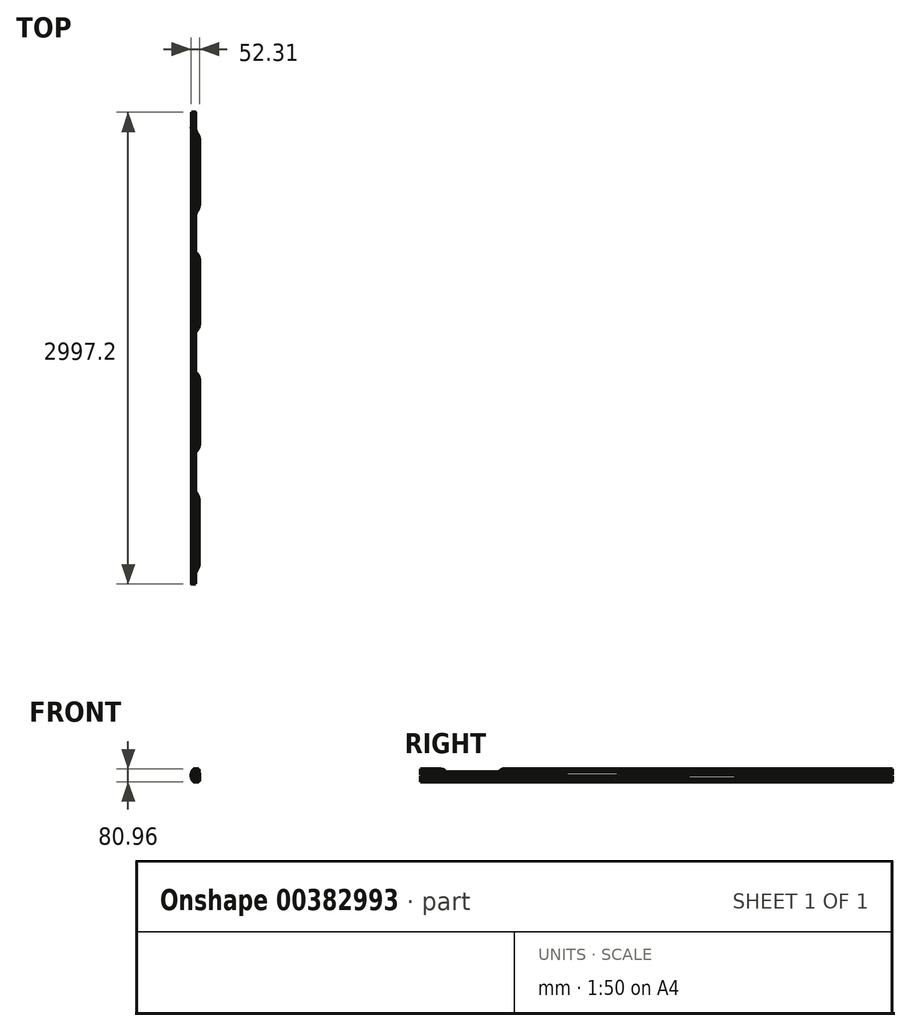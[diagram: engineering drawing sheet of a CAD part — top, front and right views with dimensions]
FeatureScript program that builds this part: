
annotation { "Feature Type Name" : "Feature", "Feature Type Description" : "" }
export const myFeature = defineFeature(function(context is Context, id is Id, definition is map)
    precondition{}
    {
        {
            var Q0;
            Q0=qCreatedBy(makeId("Front.planeOp"),FACE);
            var sketch = newSketch(context, id + "F0", { "sketchPlane" : qUnion([Q0])});
            skCircle(sketch, "E0", {"center": v(0, 0) * mm, "radius": 66.68 * mm});
            skLineSegment(sketch, "E1", {"start": v(0, 0) * mm, "end": v(0, 66.68) * mm});
            skLineSegment(sketch, "E2", {"start": v(0, 66.68) * mm, "end": v(0, 0) * mm});
            skLineSegment(sketch, "E3", {"start": v(0, -66.68) * mm, "end": v(0, 0) * mm});
            skCircle(sketch, "E4.0", {"center": v(0, 0) * mm, "radius": 53.98 * mm});
            skLineSegment(sketch, "E5", {"start": v(0, 0) * mm, "end": v(-53.98, 0) * mm});
            skLineSegment(sketch, "E6.3.0", {"start": v(0, 0) * mm, "end": v(0, -53.98) * mm});
            skLineSegment(sketch, "E6.anchor1", {"start": v(0, 0) * mm, "end": v(-53.98, 0) * mm, "construction": true});
            skLineSegment(sketch, "E6.anchor2", {"start": v(0, 0) * mm, "end": v(0, -53.98) * mm, "construction": true});
            skCircle(sketch, "E7", {"center": v(-44.21, 30.96) * mm, "radius": 9.53 * mm});
            skCircle(sketch, "E8", {"center": v(-52.7, 11.68) * mm, "radius": 9.53 * mm});
            skCircle(sketch, "E9", {"center": v(-52.7, -11.68) * mm, "radius": 9.53 * mm});
            skCircle(sketch, "E10", {"center": v(-44.21, -30.96) * mm, "radius": 9.53 * mm});
            skLineSegment(sketch, "E11", {"start": v(0, 0) * mm, "end": v(-44.21, 30.96) * mm});
            skLineSegment(sketch, "E12", {"start": v(-44.21, 30.96) * mm, "end": v(-52.02, 36.42) * mm});
            skLineSegment(sketch, "E13", {"start": v(0, 0) * mm, "end": v(-52.7, 11.68) * mm});
            skLineSegment(sketch, "E14", {"start": v(0, 0) * mm, "end": v(-52.7, -11.68) * mm});
            skLineSegment(sketch, "E15", {"start": v(0, 0) * mm, "end": v(-44.21, -30.96) * mm});
            skLineSegment(sketch, "E16", {"start": v(-44.21, -30.96) * mm, "end": v(-52.02, -36.42) * mm});
            skLineSegment(sketch, "E17", {"start": v(-44.21, 30.96) * mm, "end": v(-36.41, 25.5) * mm});
            skPoint(sketch, "E18", {"position": v(-43.4, 9.62) * mm});
            skPoint(sketch, "E19", {"position": v(-43.4, -9.62) * mm});
            skPoint(sketch, "E20", {"position": v(-36.41, -25.5) * mm});
            skArc(sketch, "E21", {"start": v(-36.41, 25.5) * mm, "mid": v(-44.45, 0) * mm, "end": v(-36.41, -25.5) * mm});
            skArc(sketch, "E22", {"start": v(-52.02, 36.42) * mm, "mid": v(-63.5, 0) * mm, "end": v(-52.02, -36.42) * mm});
            skSolve(sketch);
        }
        {
            var Q0;
            {var subQ0=sQuery(id+"F0.wireOp",EDGE,"E17");Q0=makeQuery(id+"F0.imprint","IMPRINT",FACE,{"disambiguationData":[TD([[makeQuery(id+"F0.imprint","IMPRINT",EDGE,{"derivedFrom":subQ0}),1.0]])]});}
            var Q1;
            {var subQ0=sQuery(id+"F0.wireOp",EDGE,"E12");Q1=makeQuery(id+"F0.imprint","IMPRINT",FACE,{"disambiguationData":[TD([[makeQuery(id+"F0.imprint","IMPRINT",EDGE,{"derivedFrom":subQ0}),-1.0]])]});}
            var Q2;
            {var subQ0=sQuery(id+"F0.wireOp",EDGE,"E12");Q2=makeQuery(id+"F0.imprint","IMPRINT",FACE,{"disambiguationData":[TD([[makeQuery(id+"F0.imprint","IMPRINT",EDGE,{"derivedFrom":subQ0}),1.0]])]});}
            var Q3;
            {var subQ0=sQuery(id+"F0.wireOp",EDGE,"E17");Q3=makeQuery(id+"F0.imprint","IMPRINT",FACE,{"disambiguationData":[TD([[makeQuery(id+"F0.imprint","IMPRINT",EDGE,{"derivedFrom":subQ0}),-1.0]])]});}
            var Q4;
            {var subQ0=sQuery(id+"F0.wireOp",EDGE,"E7");var subQ1=sQuery(id+"F0.wireOp",EDGE,"E4.0");var subQ2=makeQuery(id+"F0.imprint","INTERSECT",VERTEX,{"disambiguationData":[OD(1.0)],"derivedFrom":[subQ1,subQ0]});Q4=makeQuery(id+"F0.imprint","IMPRINT",FACE,{"disambiguationData":[TD([[makeQuery(id+"F0.imprint","IMPRINT",EDGE,{"disambiguationData":[TD([[subQ2,-1.0]])],"derivedFrom":subQ1}),-1.0]])]});}
            var Q5;
            {var subQ0=sQuery(id+"F0.wireOp",EDGE,"E7");var subQ1=sQuery(id+"F0.wireOp",EDGE,"E4.0");var subQ2=makeQuery(id+"F0.imprint","INTERSECT",VERTEX,{"disambiguationData":[OD(1.0)],"derivedFrom":[subQ1,subQ0]});Q5=makeQuery(id+"F0.imprint","IMPRINT",FACE,{"disambiguationData":[TD([[makeQuery(id+"F0.imprint","IMPRINT",EDGE,{"disambiguationData":[TD([[subQ2,-1.0]])],"derivedFrom":subQ1}),1.0]])]});}
            var Q6;
            {var subQ0=sQuery(id+"F0.wireOp",EDGE,"E13");var subQ1=sQuery(id+"F0.wireOp",EDGE,"E4.0");var subQ2=makeQuery(id+"F0.imprint","INTERSECT",VERTEX,{"derivedFrom":[subQ1,subQ0]});Q6=makeQuery(id+"F0.imprint","IMPRINT",FACE,{"disambiguationData":[TD([[makeQuery(id+"F0.imprint","IMPRINT",EDGE,{"disambiguationData":[TD([[subQ2,1.0]])],"derivedFrom":subQ1}),1.0]])]});}
            var Q7;
            {var subQ0=sQuery(id+"F0.wireOp",EDGE,"E4.0");var subQ1=makeQuery(id+"F0.imprint","INTERSECT",VERTEX,{"derivedFrom":[subQ0,sQuery(id+"F0.wireOp",EDGE,"E13")]});Q7=makeQuery(id+"F0.imprint","IMPRINT",FACE,{"disambiguationData":[TD([[makeQuery(id+"F0.imprint","IMPRINT",EDGE,{"disambiguationData":[TD([[subQ1,1.0]])],"derivedFrom":subQ0}),-1.0]])]});}
            var Q8;
            {var subQ0=sQuery(id+"F0.wireOp",EDGE,"E13");var subQ1=sQuery(id+"F0.wireOp",EDGE,"E4.0");var subQ2=makeQuery(id+"F0.imprint","INTERSECT",VERTEX,{"derivedFrom":[subQ1,subQ0]});Q8=makeQuery(id+"F0.imprint","IMPRINT",FACE,{"disambiguationData":[TD([[makeQuery(id+"F0.imprint","IMPRINT",EDGE,{"disambiguationData":[TD([[subQ2,-1.0]])],"derivedFrom":subQ1}),1.0]])]});}
            var Q9;
            {var subQ1=sQuery(id+"F0.wireOp",EDGE,"E4.0");var subQ8=makeQuery(id+"F0.imprint","INTERSECT",VERTEX,{"derivedFrom":[subQ1,sQuery(id+"F0.wireOp",EDGE,"E5")]});Q9=makeQuery(id+"F0.imprint","IMPRINT",FACE,{"disambiguationData":[TD([[makeQuery(id+"F0.imprint","IMPRINT",EDGE,{"disambiguationData":[TD([[subQ8,1.0]])],"derivedFrom":subQ1}),-1.0]])]});}
            var Q10;
            {var subQ0=sQuery(id+"F0.wireOp",EDGE,"E5");var subQ1=sQuery(id+"F0.wireOp",EDGE,"E4.0");var subQ2=makeQuery(id+"F0.imprint","INTERSECT",VERTEX,{"derivedFrom":[subQ1,subQ0]});Q10=makeQuery(id+"F0.imprint","IMPRINT",FACE,{"disambiguationData":[TD([[makeQuery(id+"F0.imprint","IMPRINT",EDGE,{"disambiguationData":[TD([[subQ2,1.0]])],"derivedFrom":subQ1}),1.0]])]});}
            var Q11;
            {var subQ0=sQuery(id+"F0.wireOp",EDGE,"E5");var subQ1=sQuery(id+"F0.wireOp",EDGE,"E4.0");var subQ2=makeQuery(id+"F0.imprint","INTERSECT",VERTEX,{"derivedFrom":[subQ1,subQ0]});Q11=makeQuery(id+"F0.imprint","IMPRINT",FACE,{"disambiguationData":[TD([[makeQuery(id+"F0.imprint","IMPRINT",EDGE,{"disambiguationData":[TD([[subQ2,-1.0]])],"derivedFrom":subQ1}),1.0]])]});}
            var Q12;
            {var subQ0=sQuery(id+"F0.wireOp",EDGE,"E4.0");var subQ1=makeQuery(id+"F0.imprint","INTERSECT",VERTEX,{"derivedFrom":[subQ0,sQuery(id+"F0.wireOp",EDGE,"E14")]});Q12=makeQuery(id+"F0.imprint","IMPRINT",FACE,{"disambiguationData":[TD([[makeQuery(id+"F0.imprint","IMPRINT",EDGE,{"disambiguationData":[TD([[subQ1,1.0]])],"derivedFrom":subQ0}),-1.0]])]});}
            var Q13;
            {var subQ0=sQuery(id+"F0.wireOp",EDGE,"E14");var subQ1=sQuery(id+"F0.wireOp",EDGE,"E4.0");var subQ2=makeQuery(id+"F0.imprint","INTERSECT",VERTEX,{"derivedFrom":[subQ1,subQ0]});Q13=makeQuery(id+"F0.imprint","IMPRINT",FACE,{"disambiguationData":[TD([[makeQuery(id+"F0.imprint","IMPRINT",EDGE,{"disambiguationData":[TD([[subQ2,-1.0]])],"derivedFrom":subQ1}),1.0]])]});}
            var Q14;
            {var subQ0=sQuery(id+"F0.wireOp",EDGE,"E9");var subQ1=sQuery(id+"F0.wireOp",EDGE,"E4.0");var subQ2=makeQuery(id+"F0.imprint","INTERSECT",VERTEX,{"disambiguationData":[OD(1.0)],"derivedFrom":[subQ1,subQ0]});Q14=makeQuery(id+"F0.imprint","IMPRINT",FACE,{"disambiguationData":[TD([[makeQuery(id+"F0.imprint","IMPRINT",EDGE,{"disambiguationData":[TD([[subQ2,-1.0]])],"derivedFrom":subQ1}),1.0]])]});}
            var Q15;
            {var subQ0=sQuery(id+"F0.wireOp",EDGE,"E9");var subQ1=sQuery(id+"F0.wireOp",EDGE,"E4.0");var subQ2=makeQuery(id+"F0.imprint","INTERSECT",VERTEX,{"disambiguationData":[OD(1.0)],"derivedFrom":[subQ1,subQ0]});Q15=makeQuery(id+"F0.imprint","IMPRINT",FACE,{"disambiguationData":[TD([[makeQuery(id+"F0.imprint","IMPRINT",EDGE,{"disambiguationData":[TD([[subQ2,-1.0]])],"derivedFrom":subQ1}),-1.0]])]});}
            var Q16;
            {var subQ0=sQuery(id+"F0.wireOp",EDGE,"E16");Q16=makeQuery(id+"F0.imprint","IMPRINT",FACE,{"disambiguationData":[TD([[makeQuery(id+"F0.imprint","IMPRINT",EDGE,{"derivedFrom":subQ0}),-1.0]])]});}
            var Q17;
            {var subQ1=sQuery(id+"F0.wireOp",EDGE,"E4.0");var subQ3=sQuery(id+"F0.wireOp",EDGE,"E10");var subQ4=makeQuery(id+"F0.imprint","INTERSECT",VERTEX,{"disambiguationData":[OD(0.0)],"derivedFrom":[subQ1,subQ3]});Q17=makeQuery(id+"F0.imprint","IMPRINT",FACE,{"disambiguationData":[TD([[makeQuery(id+"F0.imprint","IMPRINT",EDGE,{"disambiguationData":[TD([[subQ4,-1.0]])],"derivedFrom":subQ1}),1.0]])]});}
            var Q18;
            {var subQ1=sQuery(id+"F0.wireOp",EDGE,"E4.0");var subQ3=sQuery(id+"F0.wireOp",EDGE,"E10");var subQ4=makeQuery(id+"F0.imprint","INTERSECT",VERTEX,{"disambiguationData":[OD(1.0)],"derivedFrom":[subQ1,subQ3]});Q18=makeQuery(id+"F0.imprint","IMPRINT",FACE,{"disambiguationData":[TD([[makeQuery(id+"F0.imprint","IMPRINT",EDGE,{"disambiguationData":[TD([[subQ4,1.0]])],"derivedFrom":subQ1}),1.0]])]});}
            var Q19;
            {var subQ0=sQuery(id+"F0.wireOp",EDGE,"E16");Q19=makeQuery(id+"F0.imprint","IMPRINT",FACE,{"disambiguationData":[TD([[makeQuery(id+"F0.imprint","IMPRINT",EDGE,{"derivedFrom":subQ0}),1.0]])]});}
            var Q20;
            {var subQ0=sQuery(id+"F0.wireOp",EDGE,"E14");var subQ1=sQuery(id+"F0.wireOp",EDGE,"E4.0");var subQ2=makeQuery(id+"F0.imprint","INTERSECT",VERTEX,{"derivedFrom":[subQ1,subQ0]});Q20=makeQuery(id+"F0.imprint","IMPRINT",FACE,{"disambiguationData":[TD([[makeQuery(id+"F0.imprint","IMPRINT",EDGE,{"disambiguationData":[TD([[subQ2,1.0]])],"derivedFrom":subQ1}),1.0]])]});}
            extrude(context, id + "F1", {"entities" : qUnion([Q0, Q1, Q2, Q3, Q4, Q5, Q6, Q7, Q8, Q9, Q10, Q11, Q12, Q13, Q14, Q15, Q16, Q17, Q18, Q19, Q20]), "oppositeDirection" : true, "depth" : 3.17 * mm});
        }
        {
            var Q0;
            {var subQ0=sQuery(id+"F0.wireOp",EDGE,"E12");Q0=makeQuery(id+"F0.imprint","IMPRINT",FACE,{"disambiguationData":[TD([[makeQuery(id+"F0.imprint","IMPRINT",EDGE,{"derivedFrom":subQ0}),1.0]])]});}
            var Q1;
            {var subQ0=sQuery(id+"F0.wireOp",EDGE,"E12");Q1=makeQuery(id+"F0.imprint","IMPRINT",FACE,{"disambiguationData":[TD([[makeQuery(id+"F0.imprint","IMPRINT",EDGE,{"derivedFrom":subQ0}),-1.0]])]});}
            var Q2;
            {var subQ0=sQuery(id+"F0.wireOp",EDGE,"E17");Q2=makeQuery(id+"F0.imprint","IMPRINT",FACE,{"disambiguationData":[TD([[makeQuery(id+"F0.imprint","IMPRINT",EDGE,{"derivedFrom":subQ0}),1.0]])]});}
            var Q3;
            {var subQ0=sQuery(id+"F0.wireOp",EDGE,"E17");Q3=makeQuery(id+"F0.imprint","IMPRINT",FACE,{"disambiguationData":[TD([[makeQuery(id+"F0.imprint","IMPRINT",EDGE,{"derivedFrom":subQ0}),-1.0]])]});}
            var Q4;
            {var subQ0=sQuery(id+"F0.wireOp",EDGE,"E13");var subQ1=sQuery(id+"F0.wireOp",EDGE,"E4.0");var subQ2=makeQuery(id+"F0.imprint","INTERSECT",VERTEX,{"derivedFrom":[subQ1,subQ0]});Q4=makeQuery(id+"F0.imprint","IMPRINT",FACE,{"disambiguationData":[TD([[makeQuery(id+"F0.imprint","IMPRINT",EDGE,{"disambiguationData":[TD([[subQ2,1.0]])],"derivedFrom":subQ1}),1.0]])]});}
            var Q5;
            {var subQ0=sQuery(id+"F0.wireOp",EDGE,"E13");var subQ1=sQuery(id+"F0.wireOp",EDGE,"E4.0");var subQ2=makeQuery(id+"F0.imprint","INTERSECT",VERTEX,{"derivedFrom":[subQ1,subQ0]});Q5=makeQuery(id+"F0.imprint","IMPRINT",FACE,{"disambiguationData":[TD([[makeQuery(id+"F0.imprint","IMPRINT",EDGE,{"disambiguationData":[TD([[subQ2,-1.0]])],"derivedFrom":subQ1}),1.0]])]});}
            var Q6;
            {var subQ0=sQuery(id+"F0.wireOp",EDGE,"E4.0");var subQ1=makeQuery(id+"F0.imprint","INTERSECT",VERTEX,{"derivedFrom":[subQ0,sQuery(id+"F0.wireOp",EDGE,"E13")]});Q6=makeQuery(id+"F0.imprint","IMPRINT",FACE,{"disambiguationData":[TD([[makeQuery(id+"F0.imprint","IMPRINT",EDGE,{"disambiguationData":[TD([[subQ1,1.0]])],"derivedFrom":subQ0}),-1.0]])]});}
            var Q7;
            {var subQ0=sQuery(id+"F0.wireOp",EDGE,"E4.0");var subQ1=makeQuery(id+"F0.imprint","INTERSECT",VERTEX,{"derivedFrom":[subQ0,sQuery(id+"F0.wireOp",EDGE,"E14")]});Q7=makeQuery(id+"F0.imprint","IMPRINT",FACE,{"disambiguationData":[TD([[makeQuery(id+"F0.imprint","IMPRINT",EDGE,{"disambiguationData":[TD([[subQ1,1.0]])],"derivedFrom":subQ0}),-1.0]])]});}
            var Q8;
            {var subQ0=sQuery(id+"F0.wireOp",EDGE,"E14");var subQ1=sQuery(id+"F0.wireOp",EDGE,"E4.0");var subQ2=makeQuery(id+"F0.imprint","INTERSECT",VERTEX,{"derivedFrom":[subQ1,subQ0]});Q8=makeQuery(id+"F0.imprint","IMPRINT",FACE,{"disambiguationData":[TD([[makeQuery(id+"F0.imprint","IMPRINT",EDGE,{"disambiguationData":[TD([[subQ2,1.0]])],"derivedFrom":subQ1}),1.0]])]});}
            var Q9;
            {var subQ0=sQuery(id+"F0.wireOp",EDGE,"E14");var subQ1=sQuery(id+"F0.wireOp",EDGE,"E4.0");var subQ2=makeQuery(id+"F0.imprint","INTERSECT",VERTEX,{"derivedFrom":[subQ1,subQ0]});Q9=makeQuery(id+"F0.imprint","IMPRINT",FACE,{"disambiguationData":[TD([[makeQuery(id+"F0.imprint","IMPRINT",EDGE,{"disambiguationData":[TD([[subQ2,-1.0]])],"derivedFrom":subQ1}),1.0]])]});}
            var Q10;
            {var subQ0=sQuery(id+"F0.wireOp",EDGE,"E16");Q10=makeQuery(id+"F0.imprint","IMPRINT",FACE,{"disambiguationData":[TD([[makeQuery(id+"F0.imprint","IMPRINT",EDGE,{"derivedFrom":subQ0}),-1.0]])]});}
            var Q11;
            {var subQ0=sQuery(id+"F0.wireOp",EDGE,"E16");Q11=makeQuery(id+"F0.imprint","IMPRINT",FACE,{"disambiguationData":[TD([[makeQuery(id+"F0.imprint","IMPRINT",EDGE,{"derivedFrom":subQ0}),1.0]])]});}
            var Q12;
            {var subQ1=sQuery(id+"F0.wireOp",EDGE,"E4.0");var subQ3=sQuery(id+"F0.wireOp",EDGE,"E10");var subQ4=makeQuery(id+"F0.imprint","INTERSECT",VERTEX,{"disambiguationData":[OD(1.0)],"derivedFrom":[subQ1,subQ3]});Q12=makeQuery(id+"F0.imprint","IMPRINT",FACE,{"disambiguationData":[TD([[makeQuery(id+"F0.imprint","IMPRINT",EDGE,{"disambiguationData":[TD([[subQ4,1.0]])],"derivedFrom":subQ1}),1.0]])]});}
            var Q13;
            {var subQ1=sQuery(id+"F0.wireOp",EDGE,"E4.0");var subQ3=sQuery(id+"F0.wireOp",EDGE,"E10");var subQ4=makeQuery(id+"F0.imprint","INTERSECT",VERTEX,{"disambiguationData":[OD(0.0)],"derivedFrom":[subQ1,subQ3]});Q13=makeQuery(id+"F0.imprint","IMPRINT",FACE,{"disambiguationData":[TD([[makeQuery(id+"F0.imprint","IMPRINT",EDGE,{"disambiguationData":[TD([[subQ4,-1.0]])],"derivedFrom":subQ1}),1.0]])]});}
            extrude(context, id + "F2", {"entities" : qUnion([Q0, Q1, Q2, Q3, Q4, Q5, Q6, Q7, Q8, Q9, Q10, Q11, Q12, Q13]), "operationType" : NewBodyOperationType.ADD, "oppositeDirection" : true, "depth" : 101.6 * mm});
        }
        {
            var Q0;
            Q0=qCreatedBy(makeId("Top.planeOp"),FACE);
            var sketch = newSketch(context, id + "F3", { "sketchPlane" : qUnion([Q0])});
            skPoint(sketch, "E23.0", {"position": v(-44.21, 0) * mm});
            skPoint(sketch, "E24", {"position": v(-20.72, -76.2) * mm});
            skFitSpline(sketch, "E25", {"points": [v(-44.21, 0) * mm, v(-20.72, -76.2) * mm], "startDerivative": vector(0, -114.3) * mm, "endDerivative": vector(0, -114.3) * mm});
            skLineSegment(sketch, "E26", {"start": v(-20.72, -76.2) * mm, "end": v(-20.72, -482.6) * mm});
            skPoint(sketch, "E27", {"position": v(-44.21, -482.6) * mm});
            skPoint(sketch, "E28", {"position": v(-44.21, -520.7) * mm});
            skPoint(sketch, "E29", {"position": v(-44.21, -558.8) * mm});
            skFitSpline(sketch, "E30", {"points": [v(-44.21, -558.8) * mm, v(-20.72, -482.6) * mm], "startDerivative": vector(0, 114.3) * mm, "endDerivative": vector(0, 114.3) * mm});
            skLineSegment(sketch, "E31", {"start": v(-44.21, -558.8) * mm, "end": v(-44.21, -2895.6) * mm});
            skPoint(sketch, "E32.0", {"position": v(-52.7, 0) * mm});
            skLineSegment(sketch, "E33", {"start": v(-52.7, 0) * mm, "end": v(-52.7, -762) * mm});
            skLineSegment(sketch, "E34", {"start": v(-52.7, -762) * mm, "end": v(-52.7, -838.2) * mm});
            skLineSegment(sketch, "E35", {"start": v(-52.7, -838.2) * mm, "end": v(-20.72, -838.2) * mm});
            skLineSegment(sketch, "E36", {"start": v(-20.72, -1244.6) * mm, "end": v(-52.7, -1244.6) * mm});
            skLineSegment(sketch, "E37", {"start": v(-52.7, -1244.6) * mm, "end": v(-52.7, -2895.6) * mm});
            skLineSegment(sketch, "E38", {"start": v(-52.7, -1244.6) * mm, "end": v(-52.7, -1320.8) * mm});
            skLineSegment(sketch, "E39", {"start": v(-52.7, -1320.8) * mm, "end": v(-52.7, -2895.6) * mm});
            skFitSpline(sketch, "E40", {"points": [v(-52.7, -1320.8) * mm, v(-20.72, -1244.6) * mm], "startDerivative": vector(0, 114.3) * mm, "endDerivative": vector(0, 114.3) * mm});
            skFitSpline(sketch, "E41", {"points": [v(-20.72, -838.2) * mm, v(-52.7, -762) * mm], "startDerivative": vector(0, 114.3) * mm, "endDerivative": vector(0, 114.3) * mm});
            skLineSegment(sketch, "E42", {"start": v(-52.7, -762) * mm, "end": v(-52.7, -800.1) * mm});
            skLineSegment(sketch, "E43", {"start": v(-20.72, -838.2) * mm, "end": v(-20.72, -914.4) * mm});
            skLineSegment(sketch, "E44", {"start": v(-20.72, -1244.6) * mm, "end": v(-20.72, -1168.4) * mm});
            skLineSegment(sketch, "E45", {"start": v(-20.72, -1168.4) * mm, "end": v(-20.72, -914.4) * mm});
            skSolve(sketch);
        }
        {
            var Q0;
            {var subQ1=sQuery(id+"F0.wireOp",EDGE,"E4.0");var subQ3=sQuery(id+"F0.wireOp",EDGE,"E10");var subQ4=makeQuery(id+"F0.imprint","INTERSECT",VERTEX,{"disambiguationData":[OD(0.0)],"derivedFrom":[subQ1,subQ3]});Q0=makeQuery(id+"F0.imprint","IMPRINT",FACE,{"disambiguationData":[TD([[makeQuery(id+"F0.imprint","IMPRINT",EDGE,{"disambiguationData":[TD([[subQ4,-1.0]])],"derivedFrom":subQ1}),1.0]])]});}
            var Q1;
            {var subQ0=sQuery(id+"F0.wireOp",EDGE,"E16");Q1=makeQuery(id+"F0.imprint","IMPRINT",FACE,{"disambiguationData":[TD([[makeQuery(id+"F0.imprint","IMPRINT",EDGE,{"derivedFrom":subQ0}),-1.0]])]});}
            var Q2;
            {var subQ0=sQuery(id+"F0.wireOp",EDGE,"E16");Q2=makeQuery(id+"F0.imprint","IMPRINT",FACE,{"disambiguationData":[TD([[makeQuery(id+"F0.imprint","IMPRINT",EDGE,{"derivedFrom":subQ0}),1.0]])]});}
            var Q3;
            {var subQ1=sQuery(id+"F0.wireOp",EDGE,"E4.0");var subQ3=sQuery(id+"F0.wireOp",EDGE,"E10");var subQ4=makeQuery(id+"F0.imprint","INTERSECT",VERTEX,{"disambiguationData":[OD(1.0)],"derivedFrom":[subQ1,subQ3]});Q3=makeQuery(id+"F0.imprint","IMPRINT",FACE,{"disambiguationData":[TD([[makeQuery(id+"F0.imprint","IMPRINT",EDGE,{"disambiguationData":[TD([[subQ4,1.0]])],"derivedFrom":subQ1}),1.0]])]});}
            var Q4;
            Q4=sQuery(id+"F3.wireOp",EDGE,"E25");
            var Q5;
            Q5=sQuery(id+"F3.wireOp",EDGE,"E26");
            var Q6;
            Q6=sQuery(id+"F3.wireOp",EDGE,"E30");
            var Q7;
            Q7=sQuery(id+"F3.wireOp",EDGE,"E31");
            sweep(context, id + "F4", {"operationType" : NewBodyOperationType.ADD, "profiles" : qUnion([Q0, Q1, Q2, Q3]), "path" : qUnion([Q4, Q5, Q6, Q7])});
        }
        {
            var Q0;
            {var subQ0=sQuery(id+"F0.wireOp",EDGE,"E12");Q0=makeQuery(id+"F0.imprint","IMPRINT",FACE,{"disambiguationData":[TD([[makeQuery(id+"F0.imprint","IMPRINT",EDGE,{"derivedFrom":subQ0}),-1.0]])]});}
            var Q1;
            {var subQ0=sQuery(id+"F0.wireOp",EDGE,"E12");Q1=makeQuery(id+"F0.imprint","IMPRINT",FACE,{"disambiguationData":[TD([[makeQuery(id+"F0.imprint","IMPRINT",EDGE,{"derivedFrom":subQ0}),1.0]])]});}
            var Q2;
            {var subQ0=sQuery(id+"F0.wireOp",EDGE,"E17");Q2=makeQuery(id+"F0.imprint","IMPRINT",FACE,{"disambiguationData":[TD([[makeQuery(id+"F0.imprint","IMPRINT",EDGE,{"derivedFrom":subQ0}),-1.0]])]});}
            var Q3;
            {var subQ0=sQuery(id+"F0.wireOp",EDGE,"E17");Q3=makeQuery(id+"F0.imprint","IMPRINT",FACE,{"disambiguationData":[TD([[makeQuery(id+"F0.imprint","IMPRINT",EDGE,{"derivedFrom":subQ0}),1.0]])]});}
            var Q4;
            {var subQ0=sQuery(id+"F0.wireOp",EDGE,"E4.0");var subQ1=makeQuery(id+"F0.imprint","INTERSECT",VERTEX,{"derivedFrom":[subQ0,sQuery(id+"F0.wireOp",EDGE,"E13")]});Q4=makeQuery(id+"F0.imprint","IMPRINT",FACE,{"disambiguationData":[TD([[makeQuery(id+"F0.imprint","IMPRINT",EDGE,{"disambiguationData":[TD([[subQ1,1.0]])],"derivedFrom":subQ0}),-1.0]])]});}
            var Q5;
            {var subQ0=sQuery(id+"F0.wireOp",EDGE,"E13");var subQ1=sQuery(id+"F0.wireOp",EDGE,"E4.0");var subQ2=makeQuery(id+"F0.imprint","INTERSECT",VERTEX,{"derivedFrom":[subQ1,subQ0]});Q5=makeQuery(id+"F0.imprint","IMPRINT",FACE,{"disambiguationData":[TD([[makeQuery(id+"F0.imprint","IMPRINT",EDGE,{"disambiguationData":[TD([[subQ2,1.0]])],"derivedFrom":subQ1}),1.0]])]});}
            var Q6;
            {var subQ0=sQuery(id+"F0.wireOp",EDGE,"E13");var subQ1=sQuery(id+"F0.wireOp",EDGE,"E4.0");var subQ2=makeQuery(id+"F0.imprint","INTERSECT",VERTEX,{"derivedFrom":[subQ1,subQ0]});Q6=makeQuery(id+"F0.imprint","IMPRINT",FACE,{"disambiguationData":[TD([[makeQuery(id+"F0.imprint","IMPRINT",EDGE,{"disambiguationData":[TD([[subQ2,-1.0]])],"derivedFrom":subQ1}),1.0]])]});}
            var Q7;
            {var subQ0=sQuery(id+"F0.wireOp",EDGE,"E4.0");var subQ1=makeQuery(id+"F0.imprint","INTERSECT",VERTEX,{"derivedFrom":[subQ0,sQuery(id+"F0.wireOp",EDGE,"E14")]});Q7=makeQuery(id+"F0.imprint","IMPRINT",FACE,{"disambiguationData":[TD([[makeQuery(id+"F0.imprint","IMPRINT",EDGE,{"disambiguationData":[TD([[subQ1,1.0]])],"derivedFrom":subQ0}),-1.0]])]});}
            var Q8;
            {var subQ0=sQuery(id+"F0.wireOp",EDGE,"E14");var subQ1=sQuery(id+"F0.wireOp",EDGE,"E4.0");var subQ2=makeQuery(id+"F0.imprint","INTERSECT",VERTEX,{"derivedFrom":[subQ1,subQ0]});Q8=makeQuery(id+"F0.imprint","IMPRINT",FACE,{"disambiguationData":[TD([[makeQuery(id+"F0.imprint","IMPRINT",EDGE,{"disambiguationData":[TD([[subQ2,1.0]])],"derivedFrom":subQ1}),1.0]])]});}
            var Q9;
            {var subQ0=sQuery(id+"F0.wireOp",EDGE,"E14");var subQ1=sQuery(id+"F0.wireOp",EDGE,"E4.0");var subQ2=makeQuery(id+"F0.imprint","INTERSECT",VERTEX,{"derivedFrom":[subQ1,subQ0]});Q9=makeQuery(id+"F0.imprint","IMPRINT",FACE,{"disambiguationData":[TD([[makeQuery(id+"F0.imprint","IMPRINT",EDGE,{"disambiguationData":[TD([[subQ2,-1.0]])],"derivedFrom":subQ1}),1.0]])]});}
            extrude(context, id + "F5", {"entities" : qUnion([Q0, Q1, Q2, Q3, Q4, Q5, Q6, Q7, Q8, Q9]), "operationType" : NewBodyOperationType.ADD, "depth" : 762 * mm});
        }
        {
            var Q0;
            Q0=makeQuery(id+"F5.opExtrude","CAP_FACE",FACE,{"disambiguationData":[OSD([sQuery(id+"F0.wireOp",EDGE,"E8")])],"isStart":false});
            var Q1;
            Q1=makeQuery(id+"F5.opExtrude","CAP_FACE",FACE,{"disambiguationData":[OSD([sQuery(id+"F0.wireOp",EDGE,"E7")])],"isStart":false});
            extrude(context, id + "F6", {"entities" : qUnion([Q0, Q1]), "operationType" : NewBodyOperationType.ADD, "depth" : 762 * mm});
        }
        {
            var Q0;
            Q0=makeQuery(id+"F6.opExtrude","CAP_FACE",FACE,{"disambiguationData":[OSD([sQuery(id+"F0.wireOp",EDGE,"E7")])],"isStart":false});
            extrude(context, id + "F7", {"entities" : qUnion([Q0]), "operationType" : NewBodyOperationType.ADD, "depth" : 762 * mm});
        }
        {
            var Q0;
            Q0=qCreatedBy(makeId("Right.planeOp"),FACE);
            var sketch = newSketch(context, id + "F8", { "sketchPlane" : qUnion([Q0])});
            skPoint(sketch, "E46.0", {"position": v(-914.4, 0) * mm});
            skPoint(sketch, "E47.0", {"position": v(-838.2, 0) * mm});
            skPoint(sketch, "E48.0", {"position": v(0, 11.68) * mm});
            skPoint(sketch, "E49.0", {"position": v(0, 30.96) * mm});
            skLineSegment(sketch, "E50", {"start": v(-838.2, 11.68) * mm, "end": v(-914.4, 11.68) * mm});
            skLineSegment(sketch, "E51", {"start": v(-914.4, 11.68) * mm, "end": v(-914.4, 30.96) * mm});
            skFitSpline(sketch, "E52", {"points": [v(-838.2, 11.68) * mm, v(-914.4, 30.96) * mm], "startDerivative": vector(-114.3, 0) * mm, "endDerivative": vector(-114.3, 0) * mm});
            skFitSpline(sketch, "E53", {"points": [v(-838.2, 30.96) * mm, v(-914.4, 11.68) * mm], "startDerivative": vector(-114.3, 0) * mm, "endDerivative": vector(-114.3, 0) * mm});
            skPoint(sketch, "E54.0", {"position": v(-1206.5, 0) * mm});
            skLineSegment(sketch, "E55.0", {"start": v(-1244.6, 0) * mm, "end": v(-1168.4, 0) * mm});
            skPoint(sketch, "E56", {"position": v(-1168.4, 11.68) * mm});
            skPoint(sketch, "E57", {"position": v(-1168.4, 30.96) * mm});
            skPoint(sketch, "E58", {"position": v(-1244.6, 11.68) * mm});
            skPoint(sketch, "E59", {"position": v(-1244.6, 30.96) * mm});
            skFitSpline(sketch, "E60", {"points": [v(-1244.6, 30.96) * mm, v(-1168.4, 11.68) * mm], "startDerivative": vector(114.3, 0) * mm, "endDerivative": vector(114.3, 0) * mm});
            skSolve(sketch);
        }
        {
            var Q0;
            Q0=makeQuery(id+"F5.opExtrude","CAP_FACE",FACE,{"disambiguationData":[OSD([sQuery(id+"F0.wireOp",EDGE,"E9")])],"isStart":false});
            var Q1;
            Q1=sQuery(id+"F3.wireOp",EDGE,"E41");
            sweep(context, id + "F9", {"operationType" : NewBodyOperationType.ADD, "profiles" : qUnion([Q0]), "path" : qUnion([Q1])});
        }
        {
            var Q0;
            Q0=makeQuery(id+"F9.opSweep","CAP_FACE",FACE,{"disambiguationData":[OSD([sQuery(id+"F0.wireOp",EDGE,"E9"),sQuery(id+"F3.wireOp",VERTEX,"E41.start")])],"isStart":false});
            var Q1;
            Q1=sQuery(id+"F8.wireOp",EDGE,"E53");
            sweep(context, id + "F10", {"operationType" : NewBodyOperationType.ADD, "profiles" : qUnion([Q0]), "path" : qUnion([Q1])});
        }
        {
            var Q0;
            Q0=makeQuery(id+"F10.opSweep","CAP_FACE",FACE,{"disambiguationData":[OSD([sQuery(id+"F0.wireOp",EDGE,"E9"),sQuery(id+"F3.wireOp",VERTEX,"E41.start"),sQuery(id+"F8.wireOp",VERTEX,"E53.end")])],"isStart":false});
            var Q1;
            Q1=sQuery(id+"F3.wireOp",EDGE,"E45");
            sweep(context, id + "F11", {"operationType" : NewBodyOperationType.ADD, "profiles" : qUnion([Q0]), "path" : qUnion([Q1])});
        }
        {
            var Q0;
            Q0=makeQuery(id+"F11.opSweep","CAP_FACE",FACE,{"disambiguationData":[OSD([sQuery(id+"F0.wireOp",EDGE,"E9"),sQuery(id+"F3.wireOp",VERTEX,"E41.start"),sQuery(id+"F3.wireOp",VERTEX,"E45.start"),sQuery(id+"F8.wireOp",VERTEX,"E53.end")])],"isStart":false});
            var Q1;
            Q1=sQuery(id+"F8.wireOp",EDGE,"E60");
            sweep(context, id + "F12", {"operationType" : NewBodyOperationType.ADD, "profiles" : qUnion([Q0]), "path" : qUnion([Q1])});
        }
        {
            var Q0;
            Q0=makeQuery(id+"F12.opSweep","CAP_FACE",FACE,{"disambiguationData":[OSD([sQuery(id+"F0.wireOp",EDGE,"E9"),sQuery(id+"F3.wireOp",VERTEX,"E41.start"),sQuery(id+"F3.wireOp",VERTEX,"E45.start"),sQuery(id+"F8.wireOp",VERTEX,"E53.end"),sQuery(id+"F8.wireOp",VERTEX,"E60.start")])],"isStart":false});
            var Q1;
            Q1=sQuery(id+"F3.wireOp",EDGE,"E40");
            var Q2;
            Q2=sQuery(id+"F3.wireOp",EDGE,"E39");
            sweep(context, id + "F13", {"operationType" : NewBodyOperationType.ADD, "profiles" : qUnion([Q0]), "path" : qUnion([Q1, Q2])});
        }
        {
            var Q0;
            Q0=qCreatedBy(makeId("Top.planeOp"),FACE);
            var sketch = newSketch(context, id + "F14", { "sketchPlane" : qUnion([Q0])});
            skPoint(sketch, "E61.0", {"position": v(-52.7, 0) * mm});
            skPoint(sketch, "E62.0", {"position": v(-44.21, 0) * mm});
            skLineSegment(sketch, "E63", {"start": v(-52.7, 0) * mm, "end": v(-52.7, -1524) * mm});
            skLineSegment(sketch, "E64", {"start": v(-44.21, 0) * mm, "end": v(-44.21, -2286) * mm});
            skPoint(sketch, "E65.0", {"position": v(-20.72, -1244.6) * mm});
            skPoint(sketch, "E66", {"position": v(-20.72, -1524) * mm});
            skPoint(sketch, "E67", {"position": v(-20.72, -1600.2) * mm});
            skPoint(sketch, "E68", {"position": v(-20.72, -1676.4) * mm});
            skPoint(sketch, "E69", {"position": v(-20.72, -1930.4) * mm});
            skPoint(sketch, "E70", {"position": v(-20.72, -2006.6) * mm});
            skPoint(sketch, "E71", {"position": v(-20.72, -2082.8) * mm});
            skPoint(sketch, "E72", {"position": v(-52.7, -2082.8) * mm});
            skLineSegment(sketch, "E73", {"start": v(-20.72, -1600.2) * mm, "end": v(-20.72, -1676.4) * mm});
            skLineSegment(sketch, "E74", {"start": v(-20.72, -1930.4) * mm, "end": v(-20.72, -2006.6) * mm});
            skPoint(sketch, "E75.0", {"position": v(-52.7, -2895.6) * mm});
            skLineSegment(sketch, "E76", {"start": v(-52.7, -2082.8) * mm, "end": v(-52.7, -2895.6) * mm});
            skFitSpline(sketch, "E77", {"points": [v(-52.7, -1524) * mm, v(-20.72, -1600.2) * mm], "startDerivative": vector(0, -114.3) * mm, "endDerivative": vector(0, -114.3) * mm});
            skFitSpline(sketch, "E78", {"points": [v(-20.72, -2006.6) * mm, v(-52.7, -2082.8) * mm], "startDerivative": vector(0, -114.3) * mm, "endDerivative": vector(-0.3, -114.3) * mm});
            skLineSegment(sketch, "E79", {"start": v(-20.72, -1676.4) * mm, "end": v(-20.72, -1930.4) * mm});
            skPoint(sketch, "E80", {"position": v(-20.72, -2324.1) * mm});
            skPoint(sketch, "E81", {"position": v(-20.72, -2362.2) * mm});
            skPoint(sketch, "E82", {"position": v(-20.72, -2438.4) * mm});
            skPoint(sketch, "E83", {"position": v(-20.72, -2692.4) * mm});
            skPoint(sketch, "E84", {"position": v(-20.72, -2768.6) * mm});
            skPoint(sketch, "E85", {"position": v(-20.72, -2806.7) * mm});
            skPoint(sketch, "E86", {"position": v(-44.21, -2844.8) * mm});
            skFitSpline(sketch, "E87", {"points": [v(-44.21, -2286) * mm, v(-20.72, -2362.2) * mm], "startDerivative": vector(0, -114.3) * mm, "endDerivative": vector(0, -114.3) * mm});
            skFitSpline(sketch, "E88", {"points": [v(-20.72, -2768.6) * mm, v(-44.21, -2844.8) * mm], "startDerivative": vector(0, -114.3) * mm, "endDerivative": vector(0, -114.3) * mm});
            skLineSegment(sketch, "E89", {"start": v(-20.72, -2362.2) * mm, "end": v(-20.72, -2438.4) * mm});
            skLineSegment(sketch, "E90", {"start": v(-20.72, -2692.4) * mm, "end": v(-20.72, -2768.6) * mm});
            skLineSegment(sketch, "E91", {"start": v(-20.72, -2438.4) * mm, "end": v(-20.72, -2692.4) * mm});
            skLineSegment(sketch, "E92", {"start": v(-44.21, -2844.8) * mm, "end": v(-44.21, -2895.6) * mm});
            skSolve(sketch);
        }
        {
            var Q0;
            Q0=qCreatedBy(makeId("Right.planeOp"),FACE);
            var sketch = newSketch(context, id + "F15", { "sketchPlane" : qUnion([Q0])});
            skLineSegment(sketch, "E93.0", {"start": v(-1600.2, 0) * mm, "end": v(-1676.4, 0) * mm});
            skLineSegment(sketch, "E94.0", {"start": v(-1930.4, 0) * mm, "end": v(-2006.6, 0) * mm});
            skPoint(sketch, "E95.0", {"position": v(0, -30.96) * mm});
            skPoint(sketch, "E96.0", {"position": v(0, 11.68) * mm});
            skPoint(sketch, "E97", {"position": v(-1600.2, 11.68) * mm});
            skPoint(sketch, "E98", {"position": v(-1676.4, 11.68) * mm});
            skPoint(sketch, "E99", {"position": v(-1930.4, 11.68) * mm});
            skPoint(sketch, "E100", {"position": v(-2006.6, 11.68) * mm});
            skPoint(sketch, "E101", {"position": v(-1600.2, -30.96) * mm});
            skPoint(sketch, "E102", {"position": v(-1676.4, -30.96) * mm});
            skPoint(sketch, "E103", {"position": v(-1930.4, -30.96) * mm});
            skPoint(sketch, "E104", {"position": v(-2006.6, -30.96) * mm});
            skFitSpline(sketch, "E105", {"points": [v(-1600.2, 11.68) * mm, v(-1676.4, -30.96) * mm], "startDerivative": vector(-114.3, 0) * mm, "endDerivative": vector(-114.3, 0) * mm});
            skFitSpline(sketch, "E106", {"points": [v(-2006.6, 11.68) * mm, v(-1930.4, -30.96) * mm], "startDerivative": vector(114.3, 0) * mm, "endDerivative": vector(114.3, 0) * mm});
            skLineSegment(sketch, "E107", {"start": v(-2006.6, 11.68) * mm, "end": v(-1930.4, 11.68) * mm});
            skLineSegment(sketch, "E108", {"start": v(-1676.4, 11.68) * mm, "end": v(-1600.2, 11.68) * mm});
            skLineSegment(sketch, "E109", {"start": v(-1676.4, -30.96) * mm, "end": v(-1930.4, -30.96) * mm});
            skPoint(sketch, "E110.0", {"position": v(0, 30.96) * mm});
            skLineSegment(sketch, "E111.0", {"start": v(-2362.2, 0) * mm, "end": v(-2438.4, 0) * mm});
            skLineSegment(sketch, "E112.0", {"start": v(-2692.4, 0) * mm, "end": v(-2768.6, 0) * mm});
            skPoint(sketch, "E113", {"position": v(-2362.2, 30.96) * mm});
            skPoint(sketch, "E114", {"position": v(-2438.4, 30.96) * mm});
            skPoint(sketch, "E115", {"position": v(-2692.4, 30.96) * mm});
            skPoint(sketch, "E116", {"position": v(-2768.6, 30.96) * mm});
            skPoint(sketch, "E117", {"position": v(-2362.2, -30.96) * mm});
            skPoint(sketch, "E118", {"position": v(-2438.4, -30.96) * mm});
            skPoint(sketch, "E119", {"position": v(-2692.4, -30.96) * mm});
            skPoint(sketch, "E120", {"position": v(-2768.6, -30.96) * mm});
            skFitSpline(sketch, "E121", {"points": [v(-2362.2, 30.96) * mm, v(-2438.4, -30.96) * mm], "startDerivative": vector(-114.3, 0) * mm, "endDerivative": vector(-114.3, 0) * mm});
            skFitSpline(sketch, "E122", {"points": [v(-2768.6, 30.96) * mm, v(-2692.4, -30.96) * mm], "startDerivative": vector(114.3, 0) * mm, "endDerivative": vector(114.3, 0) * mm});
            skLineSegment(sketch, "E123", {"start": v(-2692.4, -30.96) * mm, "end": v(-2438.4, -30.96) * mm});
            skPoint(sketch, "E124", {"position": v(-2400.3, 0) * mm});
            skPoint(sketch, "E125", {"position": v(-2730.5, 0) * mm});
            skSolve(sketch);
        }
        {
            var Q0;
            Q0=makeQuery(id+"F6.opExtrude","CAP_FACE",FACE,{"disambiguationData":[OSD([sQuery(id+"F0.wireOp",EDGE,"E8")])],"isStart":false});
            var Q1;
            Q1=sQuery(id+"F14.wireOp",EDGE,"E77");
            sweep(context, id + "F16", {"operationType" : NewBodyOperationType.ADD, "profiles" : qUnion([Q0]), "path" : qUnion([Q1])});
        }
        {
            var Q0;
            Q0=makeQuery(id+"F16.opSweep","CAP_FACE",FACE,{"disambiguationData":[OSD([sQuery(id+"F0.wireOp",EDGE,"E8"),sQuery(id+"F14.wireOp",VERTEX,"E77.end")])],"isStart":false});
            var Q1;
            Q1=sQuery(id+"F15.wireOp",EDGE,"E105");
            var Q2;
            Q2=sQuery(id+"F15.wireOp",EDGE,"E109");
            var Q3;
            Q3=sQuery(id+"F15.wireOp",EDGE,"E106");
            sweep(context, id + "F17", {"operationType" : NewBodyOperationType.ADD, "profiles" : qUnion([Q0]), "path" : qUnion([Q1, Q2, Q3])});
        }
        {
            var Q0;
            Q0=makeQuery(id+"F17.opSweep","CAP_FACE",FACE,{"disambiguationData":[OSD([sQuery(id+"F0.wireOp",EDGE,"E8"),sQuery(id+"F14.wireOp",VERTEX,"E77.end"),sQuery(id+"F15.wireOp",VERTEX,"E106.start")])],"isStart":false});
            var Q1;
            Q1=sQuery(id+"F14.wireOp",EDGE,"E78");
            var Q2;
            Q2=sQuery(id+"F14.wireOp",EDGE,"E76");
            sweep(context, id + "F18", {"operationType" : NewBodyOperationType.ADD, "profiles" : qUnion([Q0]), "path" : qUnion([Q1, Q2])});
        }
        {
            var Q0;
            Q0=makeQuery(id+"F7.opExtrude","CAP_FACE",FACE,{"disambiguationData":[OSD([sQuery(id+"F0.wireOp",EDGE,"E7")])],"isStart":false});
            var Q1;
            Q1=sQuery(id+"F14.wireOp",EDGE,"E87");
            sweep(context, id + "F19", {"operationType" : NewBodyOperationType.ADD, "profiles" : qUnion([Q0]), "path" : qUnion([Q1])});
        }
        {
            var Q0;
            Q0=makeQuery(id+"F19.opSweep","CAP_FACE",FACE,{"disambiguationData":[OSD([sQuery(id+"F0.wireOp",EDGE,"E7"),sQuery(id+"F14.wireOp",VERTEX,"E87.end")])],"isStart":false});
            var Q1;
            Q1=sQuery(id+"F15.wireOp",EDGE,"E121");
            var Q2;
            Q2=sQuery(id+"F15.wireOp",EDGE,"E123");
            var Q3;
            Q3=sQuery(id+"F15.wireOp",EDGE,"E122");
            sweep(context, id + "F20", {"operationType" : NewBodyOperationType.ADD, "profiles" : qUnion([Q0]), "path" : qUnion([Q1, Q2, Q3])});
        }
        {
            var Q0;
            Q0=makeQuery(id+"F20.opSweep","CAP_FACE",FACE,{"disambiguationData":[OSD([sQuery(id+"F0.wireOp",EDGE,"E7"),sQuery(id+"F14.wireOp",VERTEX,"E87.end"),sQuery(id+"F15.wireOp",VERTEX,"E122.start")])],"isStart":false});
            var Q1;
            Q1=sQuery(id+"F14.wireOp",EDGE,"E88");
            var Q2;
            Q2=sQuery(id+"F14.wireOp",EDGE,"E92");
            sweep(context, id + "F21", {"operationType" : NewBodyOperationType.ADD, "profiles" : qUnion([Q0]), "path" : qUnion([Q1, Q2])});
        }
    });
